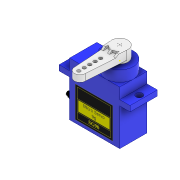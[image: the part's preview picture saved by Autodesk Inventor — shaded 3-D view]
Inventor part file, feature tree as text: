
AUTODESK INVENTOR PART (.ipt)
format: ipt  version: 2022 (Build 260153000, 153)  size: 390,656 bytes
history: native  units: mm
features: sketch x19, extrude x13, other x5, plane x3, split x1, loft x1, projected_geometry x1
ambient origin geometry x8: Origin, YZ Plane, XZ Plane, XY Plane, X Axis, Y Axis, Z Axis, Center Point
bodies: Solid1 (feature_tree), Solid4 (feature_tree), Solid2 (feature_tree), Solid3 (feature_tree)
feature tree (43):
  extrude  "Extrusion1"  Depth=12.5mm
  extrude  "Extrusion2"  Depth=11.5mm
  extrude  "Extrusion3"  Depth=32.5mm
  extrude  "Extrusion4"  Depth=2.5mm TaperAngle=0.0deg
  extrude  "Extrusion5"  Depth=2.0mm
  extrude  "Extrusion6"  Depth=3.0mm
  extrude  "Extrusion7"  Depth=6.25mm
  plane  "Work Plane1"
  extrude  "Extrusion8"  Depth=5.0mm
  extrude  "Extrusion9"  Depth=0.5mm TaperAngle=0.0deg
  extrude  "Extrusion10"  Depth=5.0mm TaperAngle=0.0deg
  sketch  "Sketch13"  dims[d27=-1.0mm d28=22.0mm]
  plane  "Work Plane2"
  extrude  "Extrusion11"  Depth=22.0mm
  split  "Split1"
  other  "Decal1"
  other  "Decal2"
  extrude  "Extrusion12"  Depth=2.0mm
  extrude  "Extrusion13"  Depth=2.5mm
  plane  "Work Plane3"
  loft  "Loft1"
  sketch  "Sketch21"  dims[d39=1.5mm d40=3.0mm d41=0.0mm d42=3.5mm d43=1.0mm d44=0.0mm d45=4.732526mm d46=3.5mm d47=4.733mm d48=0.0mm d49=1.0mm d50=0.0mm d51=1.0mm d52=0.0mm d67=6.25mm d68=4.0mm d69=1.3mm d70=0.65mm d71=0.65mm d72=3.0mm d73=0.0mm d74=1.0mm d75=0.0mm d76=3.0mm d77=1.88mm d78=0.0mm d79=90.0deg d80=0.0mm d81=90.0deg]
  sketch  "Sketch1"  dims[d0=23.0mm d1=12.5mm]
  sketch  "Sketch2"  dims[d2=17.0mm d3=0.0mm d4=11.5mm]
  sketch  "Sketch3"  dims[d5=6.25mm d6=32.5mm]
  sketch  "Sketch4"  dims[d7=2.5mm d8=0.0mm d9=5.0mm d10=0.0mm]
  sketch  "Sketch5"  dims[d11=2.0mm d12=2.0mm]
  sketch  "Sketch7"  dims[d13=3.0mm d14=3.0mm]
  sketch  "Sketch8"  dims[d15=5.0mm d16=0.0mm d17=6.25mm]
  sketch  "Sketch9"  dims[d18=5.0mm d19=0.0mm d20=5.0mm]
  sketch  "Sketch10"  dims[d21=5.0mm d22=0.5mm d23=0.0mm]
  sketch  "Sketch12"  dims[d24=7.5mm d25=5.0mm d26=0.0mm]
  sketch  "Sketch14"  dims[d29=5.0mm d30=2.0mm]
  sketch  "Sketch15"  dims[d31=2.5mm d32=2.5mm]
  sketch  "Sketch16"  dims[d33=2.5mm d34=2.5mm]
  other  "Image1"
  sketch  "Sketch17"  dims[d35=1.5mm]
  other  "Image2"
  sketch  "Sketch18"  dims[d36=1.5mm]
  sketch  "Sketch19"  dims[d37=1.5mm]
  projected_geometry  "Projected Loop1"
  sketch  "Sketch20"  dims[d38=1.5mm]
  other  "Edges1"
